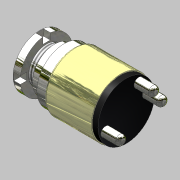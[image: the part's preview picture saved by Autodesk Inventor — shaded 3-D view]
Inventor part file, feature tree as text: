
AUTODESK INVENTOR PART (.ipt)
format: ipt  version: unknown  size: 296,448 bytes
history: native  units: mm
features: sketch x6, extrude x5, fillet x2, chamfer x2, revolve x1, thread x1, plane x1, pattern_circular x1, other x1
ambient origin geometry x8: Origin, YZ Plane, XZ Plane, XY Plane, X Axis, Y Axis, Z Axis, Center Point
feature tree (20):
  revolve  "Revolution1"  [1 undecoded]
  thread  "Thread1"  [1 undecoded]
  plane  "Work Plane1"
  extrude  "Extrusion3"  Depth=3.0mm
  fillet  "Fillet2"  Radius=9.8mm
  fillet  "Fillet3"  [1 undecoded]
  chamfer  "Chamfer1"  Distance=10.0mm
  extrude  "Extrusion4"  Depth=5.0mm
  extrude  "Extrusion5"  Depth=5.0mm
  extrude  "Extrusion6"  Depth=2.0mm
  chamfer  "Chamfer2"  Distance=5.0mm
  extrude  "Extrusion7"  Depth=5.0mm
  pattern_circular  "Circular Pattern2"  [2 undecoded]
  sketch  "Sketch1"  dims[d0=19.0mm d1=31.0mm d2=23.5mm]
  other  "Work Axis1"
  sketch  "Sketch5"  dims[d3=30.0mm d6=3.0mm d8=9.8mm d10=90.0deg d14=10.0mm d15=0.0mm]
  sketch  "Sketch6"  dims[d16=0.0mm d29=5.0mm]
  sketch  "Sketch7"  dims[d30=5.0mm d31=5.0mm]
  sketch  "Sketch8"  dims[d32=9.5mm d33=0.0mm d34=2.0mm]
  sketch  "Sketch9"  dims[d35=28.8mm d36=5.0mm d37=5.0mm d38=28.0mm d39=1.0mm d40=0.3mm d41=2.0mm d42=45.0deg d43=10.0mm d44=2.0mm d45=0.0mm d46=2.0mm d47=0.0mm d48=19.2mm d49=28.0mm d50=5.5mm d51=0.0mm d52=3.0mm d53=2.0mm d54=30.0deg d55=4.0mm d56=2.0mm d57=3.5mm d58=0.0mm d59=40.0mm d60=360.0deg]
note: 5 required parameter values undecoded (feature->parameter linkage not recoverable at this tier; creation-order binding heuristic only, values carry confidence <= 0.55)